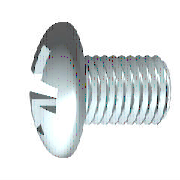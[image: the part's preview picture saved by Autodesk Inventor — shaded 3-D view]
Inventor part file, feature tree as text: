
AUTODESK INVENTOR PART (.ipt)
format: ipt  version: 2022.1 (Build 261234000, 234)  size: 280,576 bytes
history: native  units: mm (DEFAULTED — no unit token found)
features: other x2, plane x2, extrude x1
ambient origin geometry x7: Origin, YZ Plane, XZ Plane, X Axis, Y Axis, Z Axis, Center Point
bodies: Solid1 (feature_tree)
feature tree (5):
  other  "Cuerpo"
  plane  "Work Plane1"
  extrude  "Ranura"  Depth=8.0mm
  other  "Corte"
  plane  "Work Plane3"
